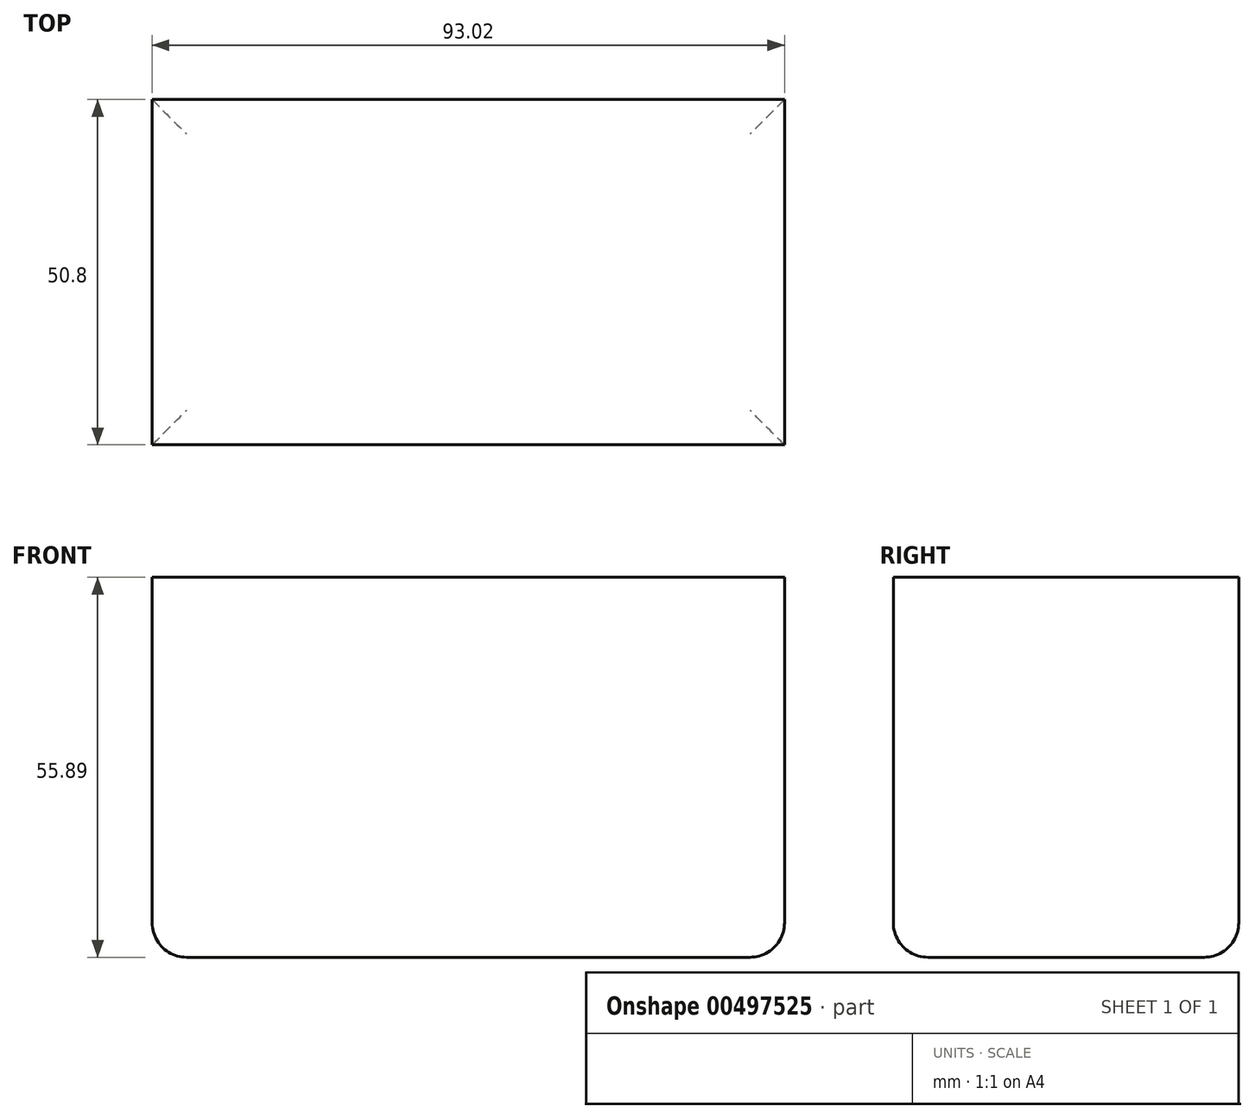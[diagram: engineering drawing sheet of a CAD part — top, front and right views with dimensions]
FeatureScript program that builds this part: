
annotation { "Feature Type Name" : "Feature", "Feature Type Description" : "" }
export const myFeature = defineFeature(function(context is Context, id is Id, definition is map)
    precondition{}
    {
        {
            var Q0;
            Q0=qCreatedBy(makeId("Front.planeOp"),FACE);
            var sketch = newSketch(context, id + "F0", { "sketchPlane" : qUnion([Q0])});
            skLineSegment(sketch, "E0.bottom", {"start": v(-45.07, -27.55) * mm, "end": v(47.95, -27.55) * mm});
            skLineSegment(sketch, "E0.top", {"start": v(-45.07, 28.34) * mm, "end": v(47.95, 28.34) * mm});
            skLineSegment(sketch, "E0.left", {"start": v(-45.07, -27.55) * mm, "end": v(-45.07, 28.34) * mm});
            skLineSegment(sketch, "E0.right", {"start": v(47.95, -27.55) * mm, "end": v(47.95, 28.34) * mm});
            skSolve(sketch);
        }
        {
            var Q0;
            Q0=makeQuery(id+"F0.imprint","IMPRINT",FACE,{"disambiguationData":[TD([[makeQuery(id+"F0.imprint","IMPRINT",EDGE,{"derivedFrom":sQuery(id+"F0.wireOp",EDGE,"E0.bottom")}),1.0]])]});
            extrude(context, id + "F1", {"entities" : qUnion([Q0]), "depth" : 50.8 * mm});
        }
        {
            var Q0;
            Q0=makeQuery(id+"F1.opExtrude","SWEPT_FACE",FACE,{"disambiguationData":[OSD([sQuery(id+"F0.wireOp",EDGE,"E0.bottom")])]});
            fillet(context, id + "F2", {"entities" : qUnion([Q0]), "radius" : 5.08 * mm, "tangentPropagation" : true, "allowEdgeOverflow" : false});
        }
    });
